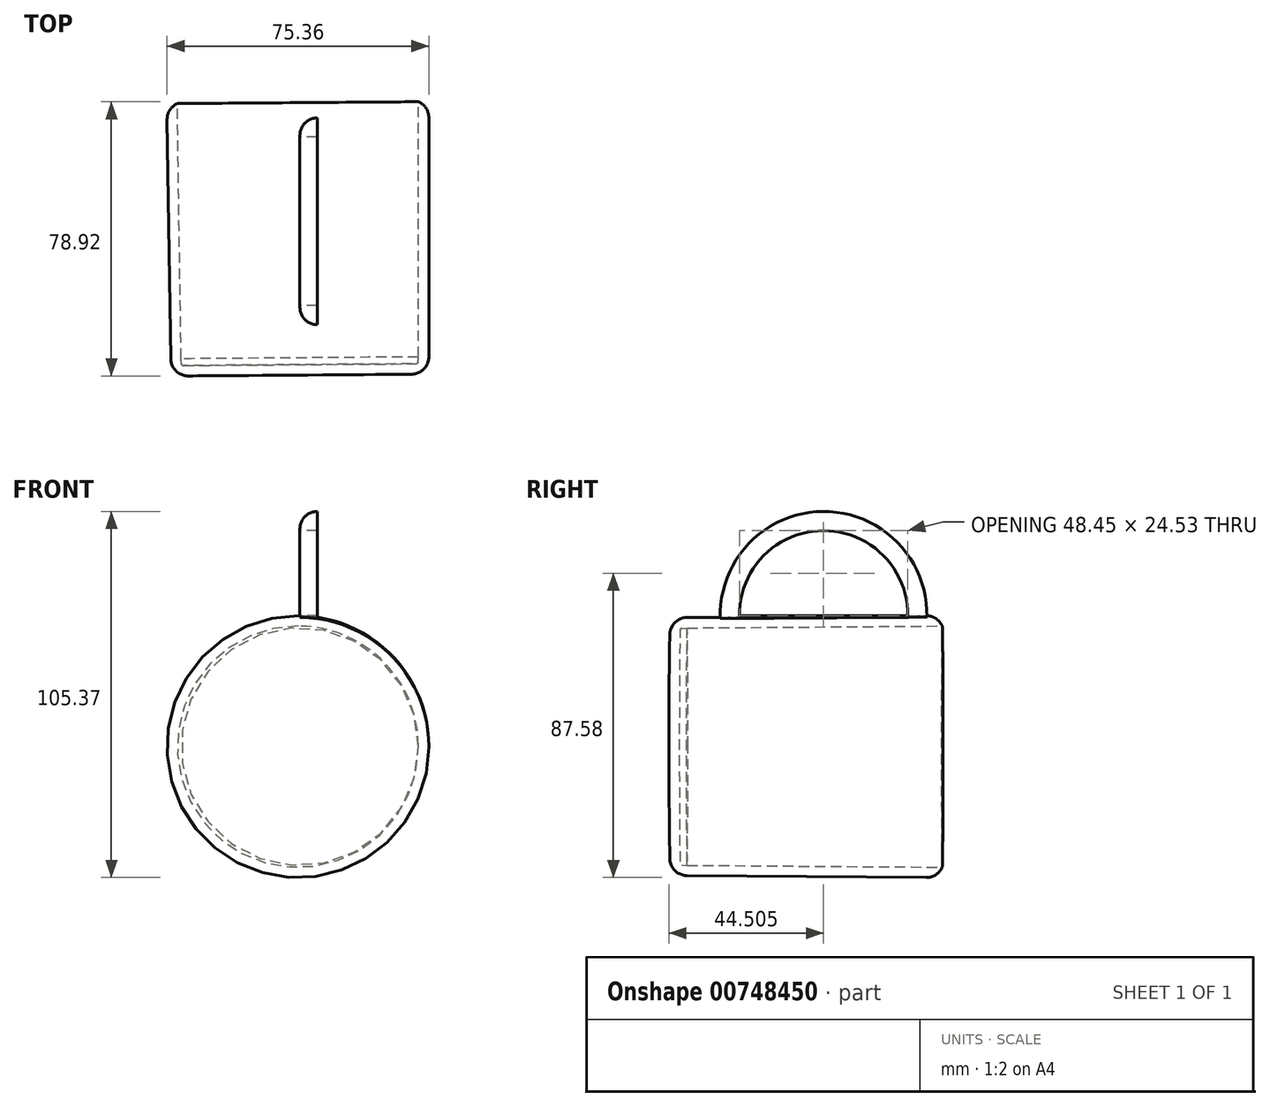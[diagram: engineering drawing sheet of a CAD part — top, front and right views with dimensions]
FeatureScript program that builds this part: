
annotation { "Feature Type Name" : "Feature", "Feature Type Description" : "" }
export const myFeature = defineFeature(function(context is Context, id is Id, definition is map)
    precondition{}
    {
        {
            var Q0;
            Q0=qCreatedBy(makeId("Top.planeOp"),FACE);
            var sketch = newSketch(context, id + "F0", { "sketchPlane" : qUnion([Q0])});
            skLineSegment(sketch, "E0", {"start": v(37.12, 42.27) * mm, "end": v(37.12, -31.16) * mm});
            skLineSegment(sketch, "E1", {"start": v(0, -36.4) * mm, "end": v(32.16, -36.16) * mm});
            skPoint(sketch, "E2.visualSharp", {"position": v(37.12, -36.12) * mm});
            skArc(sketch, "E2.filletArc", {"start": v(32.16, -36.16) * mm, "mid": v(35.67, -34.68) * mm, "end": v(37.12, -31.16) * mm});
            skLineSegment(sketch, "E3.0", {"start": v(34.12, 42.27) * mm, "end": v(34.12, -31.19) * mm});
            skLineSegment(sketch, "E4.0", {"start": v(-0.02, -33.4) * mm, "end": v(32.16, -33.16) * mm});
            skLineSegment(sketch, "E5", {"start": v(32.16, -33.16) * mm, "end": v(33.52, -33.16) * mm});
            skLineSegment(sketch, "E6", {"start": v(34.02, -32.7) * mm, "end": v(34.12, -31.19) * mm});
            skPoint(sketch, "E7.visualSharp", {"position": v(34, -33.16) * mm});
            skArc(sketch, "E7.filletArc", {"start": v(33.9, -33.16) * mm, "mid": v(33.96, -33.13) * mm, "end": v(34, -33.07) * mm});
            skArc(sketch, "E8.filletArc", {"start": v(33.52, -33.16) * mm, "mid": v(33.86, -33.03) * mm, "end": v(34.02, -32.7) * mm});
            skLineSegment(sketch, "E9", {"start": v(34.12, 42.27) * mm, "end": v(37.12, 42.27) * mm});
            skLineSegment(sketch, "E10", {"start": v(0, -36.4) * mm, "end": v(-0.6, 42.27) * mm});
            skSolve(sketch);
        }
        {
            var Q0;
            Q0=makeQuery(id+"F0.imprint","IMPRINT",FACE,{"disambiguationData":[TD([[makeQuery(id+"F0.imprint","IMPRINT",EDGE,{"derivedFrom":sQuery(id+"F0.wireOp",EDGE,"E0")}),-1.0]])]});
            var Q1;
            Q1=sQuery(id+"F0.wireOp",EDGE,"E10");
            revolve(context, id + "F1", {"surfaceOperationType" : NewSurfaceOperationType.NEW, "entities" : qUnion([Q0]), "axis" : qUnion([Q1]), "revolveType" : RevolveType.FULL});
        }
        {
            var Q0;
            Q0=qCreatedBy(makeId("Right.planeOp"),FACE);
            var sketch = newSketch(context, id + "F2", { "sketchPlane" : qUnion([Q0])});
            skArc(sketch, "E11", {"start": v(37.56, 36.32) * mm, "mid": v(7.85, 67.69) * mm, "end": v(-21.85, 36.32) * mm});
            skArc(sketch, "E12.0", {"start": v(32.55, 36.32) * mm, "mid": v(7.85, 62.69) * mm, "end": v(-16.84, 36.32) * mm});
            skLineSegment(sketch, "E13", {"start": v(37.56, 36.32) * mm, "end": v(-21.85, 36.32) * mm});
            skSolve(sketch);
        }
        {
            var Q0;
            Q0 = qSketchRegion(id + "F2", true);
            extrude(context, id + "F3", {"entities" : qUnion([Q0]), "operationType" : NewBodyOperationType.ADD, "depth" : 5 * mm, "offsetDistance" : 25 * mm});
        }
        {
            var Q0;
            Q0=makeQuery(id+"F3.opExtrude","CAP_FACE",FACE,{"disambiguationData":[OSD([sQuery(id+"F2.wireOp",EDGE,"E11"),sQuery(id+"F2.wireOp",EDGE,"E13")])],"isStart":true});
            var sketch = newSketch(context, id + "F4", { "sketchPlane" : qUnion([Q0])});
            skArc(sketch, "E14", {"start": v(16.37, 37.63) * mm, "mid": v(-7.85, 62.17) * mm, "end": v(-32.08, 37.63) * mm});
            skLineSegment(sketch, "E15", {"start": v(-32.08, 37.63) * mm, "end": v(16.37, 37.63) * mm});
            skSolve(sketch);
        }
        {
            var Q0;
            Q0 = qSketchRegion(id + "F4", true);
            extrude(context, id + "F5", {"entities" : qUnion([Q0]), "operationType" : NewBodyOperationType.REMOVE, "oppositeDirection" : true, "depth" : 25 * mm, "offsetDistance" : 25 * mm});
        }
        {
            var Q0;
            Q0=makeQuery(id+"F1.opRevolve","SWEPT_EDGE",EDGE,{"disambiguationData":[OSD([sQuery(id+"F0.wireOp",EDGE,"E0"),sQuery(id+"F0.wireOp",EDGE,"E9")])]});
            fillet(context, id + "F6", {"entities" : qUnion([Q0]), "radius" : 5 * mm, "tangentPropagation" : true, "allowEdgeOverflow" : false});
        }
        {
            var Q0;
            Q0=makeQuery(id+"F3.opExtrude","CAP_EDGE",EDGE,{"disambiguationData":[OSD([sQuery(id+"F2.wireOp",EDGE,"E11")])],"isStart":true});
            fillet(context, id + "F7", {"entities" : qUnion([Q0]), "radius" : 5 * mm, "tangentPropagation" : true, "allowEdgeOverflow" : false});
        }
    });
